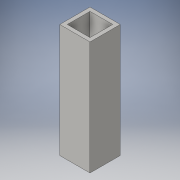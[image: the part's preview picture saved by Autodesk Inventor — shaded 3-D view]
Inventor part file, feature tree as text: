
AUTODESK INVENTOR PART (.ipt)
format: ipt  version: 2016 (Build 200138000, 138)  size: 95,232 bytes
history: native  units: in
note: dims shown in document units (in); Inventor stores cm internally (conversion verified against a paired STEP export)
features: extrude x1, sketch x1
ambient origin geometry x8: Origin, YZ Plane, XZ Plane, XY Plane, X Axis, Y Axis, Z Axis, Center Point
bodies: Solid1 (feature_tree)
feature tree (2):
  extrude  "Extrusion1"  Depth=1.0in
  sketch  "Sketch1"  dims[d0=1.0in d1=1.0in d2=0.125in d3=0.125in d4=0.125in d5=0.125in d6=3.75in d7=0.0in]
